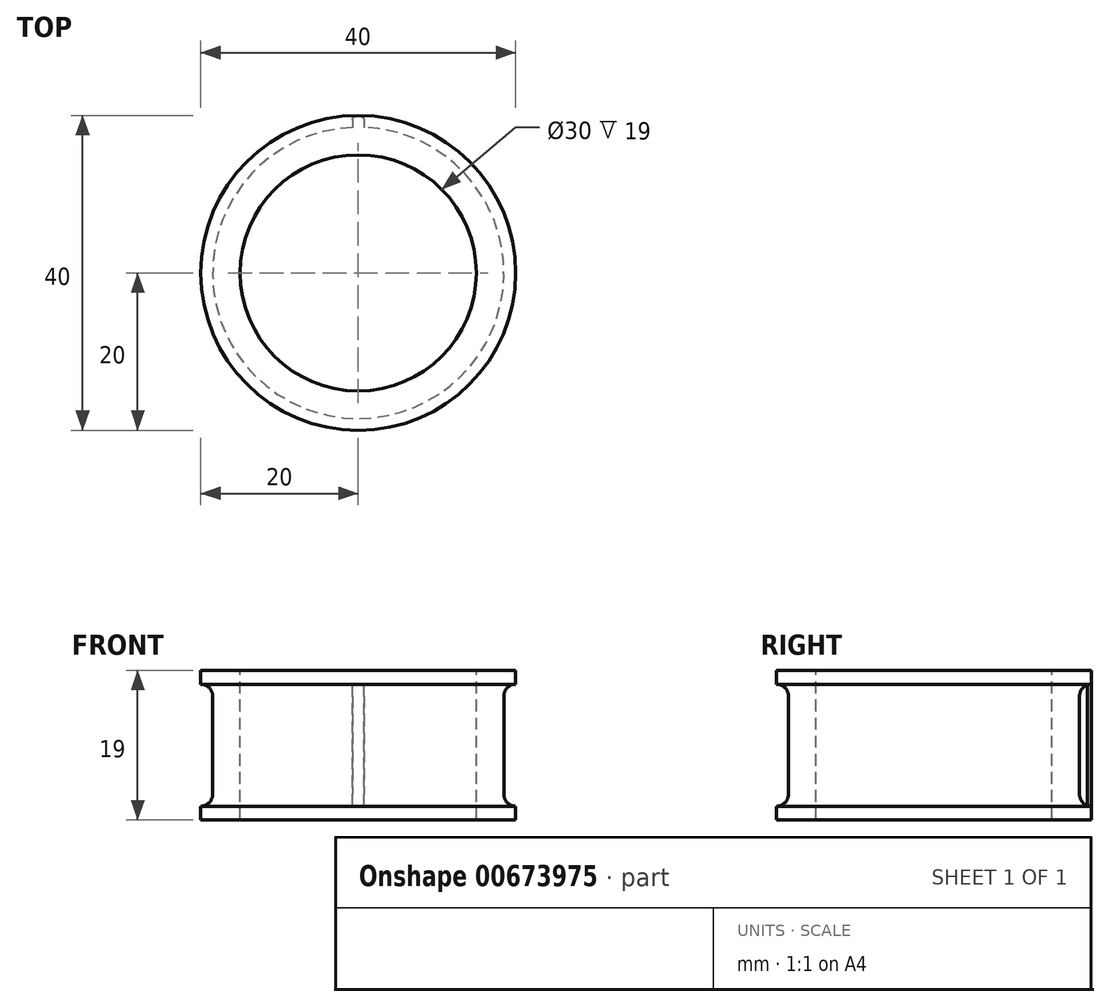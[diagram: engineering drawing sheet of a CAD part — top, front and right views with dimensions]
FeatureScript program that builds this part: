
annotation { "Feature Type Name" : "Feature", "Feature Type Description" : "" }
export const myFeature = defineFeature(function(context is Context, id is Id, definition is map)
    precondition{}
    {
        {
            var Q0;
            Q0=qCreatedBy(makeId("Top.planeOp"),FACE);
            var sketch = newSketch(context, id + "F0", { "sketchPlane" : qUnion([Q0])});
            skCircle(sketch, "E0", {"center": v(0, 0) * mm, "radius": 20 * mm});
            skSolve(sketch);
        }
        {
            var Q0;
            Q0=makeQuery(id+"F0.imprint","IMPRINT",FACE,{"disambiguationData":[TD([[makeQuery(id+"F0.imprint","IMPRINT",EDGE,{"derivedFrom":sQuery(id+"F0.wireOp",EDGE,"E0")}),1.0]])]});
            extrude(context, id + "F1", {"entities" : qUnion([Q0]), "depth" : 19 * mm, "offsetDistance" : 25 * mm});
        }
        {
            var Q0;
            Q0=qCreatedBy(makeId("Front.planeOp"),FACE);
            var sketch = newSketch(context, id + "F2", { "sketchPlane" : qUnion([Q0])});
            skLineSegment(sketch, "E1.bottom", {"start": v(-20, 17.25) * mm, "end": v(-18.5, 17.25) * mm});
            skLineSegment(sketch, "E1.top", {"start": v(-20, 1.75) * mm, "end": v(-18.5, 1.75) * mm});
            skLineSegment(sketch, "E1.left", {"start": v(-20, 17.25) * mm, "end": v(-20, 1.75) * mm});
            skLineSegment(sketch, "E1.right", {"start": v(-18.5, 17.25) * mm, "end": v(-18.5, 1.75) * mm});
            skLineSegment(sketch, "E2", {"start": v(0, 59.24) * mm, "end": v(0, -12.61) * mm, "construction": true});
            skSolve(sketch);
        }
        {
            var Q0;
            Q0=makeQuery(id+"F2.imprint","IMPRINT",FACE,{"disambiguationData":[TD([[makeQuery(id+"F2.imprint","IMPRINT",EDGE,{"derivedFrom":sQuery(id+"F2.wireOp",EDGE,"E1.bottom")}),-1.0]])]});
            var Q1;
            Q1=sQuery(id+"F2.wireOp",EDGE,"E2");
            revolve(context, id + "F3", {"operationType" : NewBodyOperationType.REMOVE, "entities" : qUnion([Q0]), "axis" : qUnion([Q1]), "revolveType" : RevolveType.FULL, "oppositeDirection" : true});
        }
        {
            var Q0;
            Q0=makeQuery(id+"F1.opExtrude","CAP_FACE",FACE,{"disambiguationData":[OSD([sQuery(id+"F0.wireOp",EDGE,"E0")])],"isStart":false});
            var sketch = newSketch(context, id + "F4", { "sketchPlane" : qUnion([Q0])});
            skLineSegment(sketch, "E3.bottom", {"start": v(-0.75, 0) * mm, "end": v(0.75, 0) * mm});
            skLineSegment(sketch, "E3.left", {"start": v(-0.75, 0) * mm, "end": v(-0.75, 19.47) * mm});
            skLineSegment(sketch, "E3.right", {"start": v(0.75, 0) * mm, "end": v(0.75, 19.47) * mm});
            skArc(sketch, "E4", {"start": v(0.75, 19.47) * mm, "mid": v(0, 20) * mm, "end": v(-0.75, 19.47) * mm});
            skLineSegment(sketch, "E5", {"start": v(-0.75, 19.47) * mm, "end": v(0.75, 19.47) * mm, "construction": true});
            skPoint(sketch, "E6", {"position": v(0, 20) * mm});
            skLineSegment(sketch, "E7", {"start": v(-0.75, 19.37) * mm, "end": v(0.75, 19.37) * mm});
            skSolve(sketch);
        }
        {
            var Q0;
            Q0=makeQuery(id+"F3.boolean.opBoolean","COPY",EDGE,{"derivedFrom":makeQuery(id+"F3.opRevolve","SWEPT_EDGE",EDGE,{"disambiguationData":[OSD([sQuery(id+"F2.wireOp",EDGE,"E1.bottom"),sQuery(id+"F2.wireOp",EDGE,"E1.right")])]})});
            var Q1;
            Q1=makeQuery(id+"F3.boolean.opBoolean","COPY",EDGE,{"derivedFrom":makeQuery(id+"F3.opRevolve","SWEPT_EDGE",EDGE,{"disambiguationData":[OSD([sQuery(id+"F2.wireOp",EDGE,"E1.top"),sQuery(id+"F2.wireOp",EDGE,"E1.right")])]})});
            fillet(context, id + "F5", {"entities" : qUnion([Q0, Q1]), "radius" : 1.5 * mm, "tangentPropagation" : true, "allowEdgeOverflow" : false});
        }
        {
            var Q0;
            {var subQ6=sQuery(id+"F4.wireOp",EDGE,"E7");Q0=makeQuery(id+"F4.imprint","IMPRINT",FACE,{"disambiguationData":[TD([[makeQuery(id+"F4.imprint","IMPRINT",EDGE,{"derivedFrom":subQ6}),1.0]])]});}
            var Q1;
            {var subQ0=sQuery(id+"F4.wireOp",EDGE,"E3.bottom");Q1=makeQuery(id+"F4.imprint","IMPRINT",FACE,{"disambiguationData":[TD([[makeQuery(id+"F4.imprint","IMPRINT",EDGE,{"derivedFrom":subQ0}),1.0]])]});}
            extrude(context, id + "F6", {"entities" : qUnion([Q0, Q1]), "operationType" : NewBodyOperationType.ADD, "oppositeDirection" : true, "depth" : 19 * mm, "offsetDistance" : 25 * mm});
        }
        {
            var Q0;
            Q0=makeQuery(id+"F1.opExtrude","CAP_FACE",FACE,{"disambiguationData":[OSD([sQuery(id+"F0.wireOp",EDGE,"E0")])],"isStart":false});
            var sketch = newSketch(context, id + "F7", { "sketchPlane" : qUnion([Q0])});
            skCircle(sketch, "E8.0", {"center": v(0, 0) * mm, "radius": 15 * mm});
            skSolve(sketch);
        }
        {
            var Q0;
            Q0=makeQuery(id+"F7.imprint","IMPRINT",FACE,{"disambiguationData":[TD([[makeQuery(id+"F7.imprint","IMPRINT",EDGE,{"derivedFrom":sQuery(id+"F7.wireOp",EDGE,"E8.0")}),1.0]])]});
            extrude(context, id + "F8", {"entities" : qUnion([Q0]), "operationType" : NewBodyOperationType.REMOVE, "endBound" : BoundingType.THROUGH_ALL, "oppositeDirection" : true, "depth" : 25 * mm, "offsetDistance" : 25 * mm});
        }
    });
